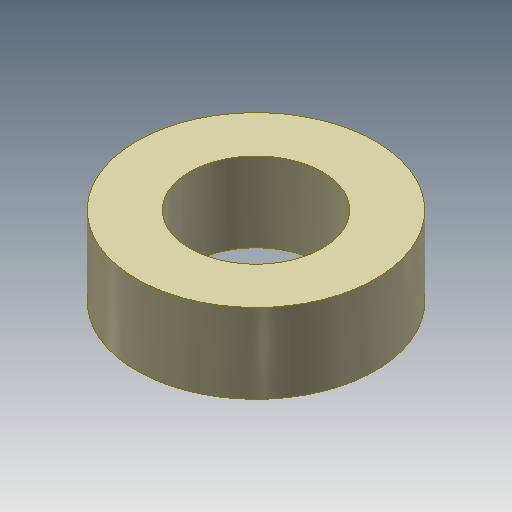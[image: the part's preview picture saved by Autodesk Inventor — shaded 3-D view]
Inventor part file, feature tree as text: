
AUTODESK INVENTOR PART (.ipt)
format: ipt  version: 2020.2 (Build 242310000, 310)  size: 93,696 bytes
history: native  units: mm
features: extrude x1, sketch x1
ambient origin geometry x8: Origin, YZ Plane, XZ Plane, XY Plane, X Axis, Y Axis, Z Axis, Center Point
bodies: Body1 (feature_tree)
feature tree (2):
  extrude  "Extrusion7"  Depth=3.0mm
  sketch  "Sketch11"  dims[d82=5.0mm d83=9.0mm d84=3.0mm d85=0.0mm]
